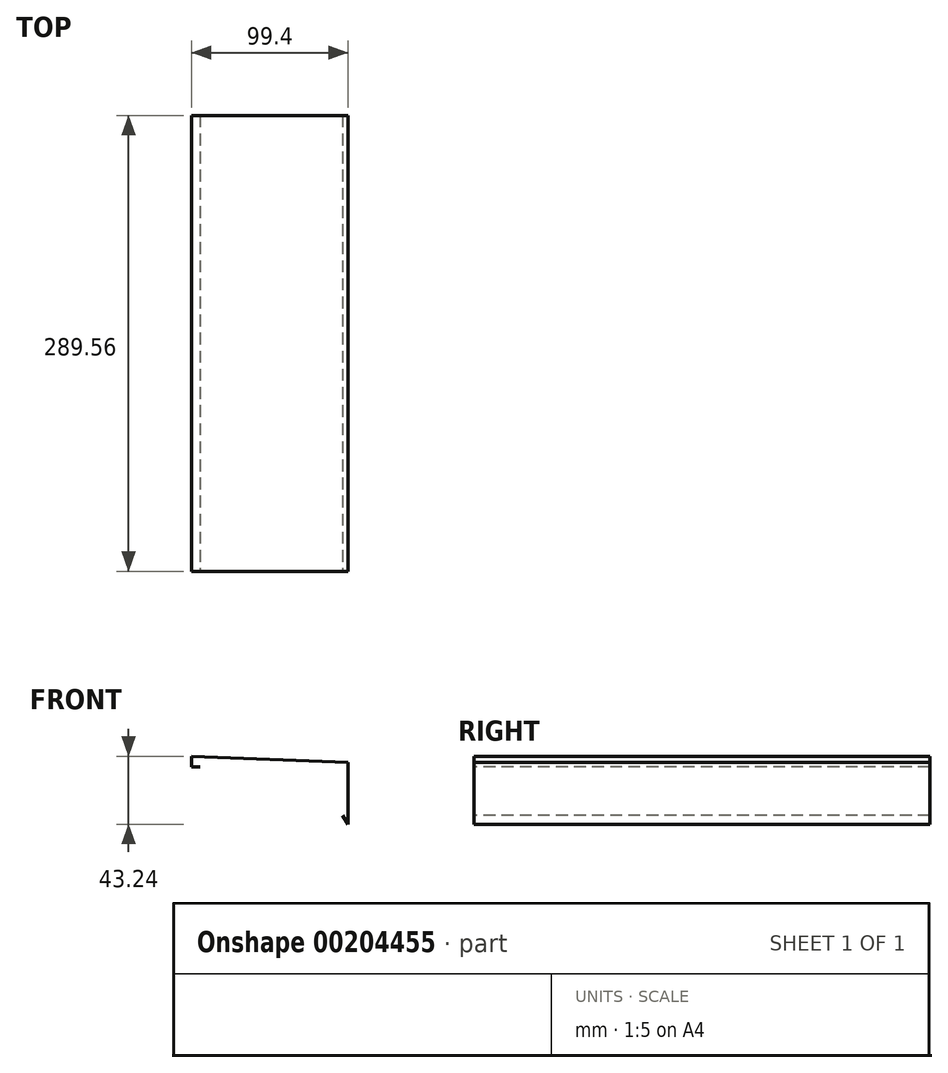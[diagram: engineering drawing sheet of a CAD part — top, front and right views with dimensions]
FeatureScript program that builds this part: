
annotation { "Feature Type Name" : "Feature", "Feature Type Description" : "" }
export const myFeature = defineFeature(function(context is Context, id is Id, definition is map)
    precondition{}
    {
        {
            var Q0;
            Q0=qCreatedBy(makeId("Front.planeOp"),FACE);
            var sketch = newSketch(context, id + "F0", { "sketchPlane" : qUnion([Q0])});
            skLineSegment(sketch, "E0", {"start": v(-46.76, 11.16) * mm, "end": v(-52.17, 11.16) * mm});
            skLineSegment(sketch, "E1", {"start": v(-52.17, 11.16) * mm, "end": v(-52.17, 17.74) * mm});
            skLineSegment(sketch, "E2", {"start": v(-52.17, 17.74) * mm, "end": v(47.23, 13.98) * mm});
            skLineSegment(sketch, "E3", {"start": v(47.23, 13.98) * mm, "end": v(47.23, -25.5) * mm});
            skLineSegment(sketch, "E4", {"start": v(47.23, -25.5) * mm, "end": v(43.7, -19.62) * mm});
            skSolve(sketch);
        }
        {
            var Q0;
            Q0 = qSketchRegion(id + "F0", true);
            var Q1;
            Q1=sQuery(id+"F0.wireOp",EDGE,"E2");
            var Q2;
            Q2=sQuery(id+"F0.wireOp",EDGE,"E3");
            var Q3;
            Q3=sQuery(id+"F0.wireOp",EDGE,"E4");
            var Q4;
            Q4=sQuery(id+"F0.wireOp",EDGE,"E0");
            var Q5;
            Q5=sQuery(id+"F0.wireOp",EDGE,"E1");
            extrude(context, id + "F1", {"entities" : qUnion([Q0]), "bodyType" : ToolBodyType.SURFACE, "surfaceEntities" : qUnion([Q1, Q2, Q3, Q4, Q5]), "endBound" : BoundingType.SYMMETRIC, "depth" : 289.56 * mm});
        }
    });
